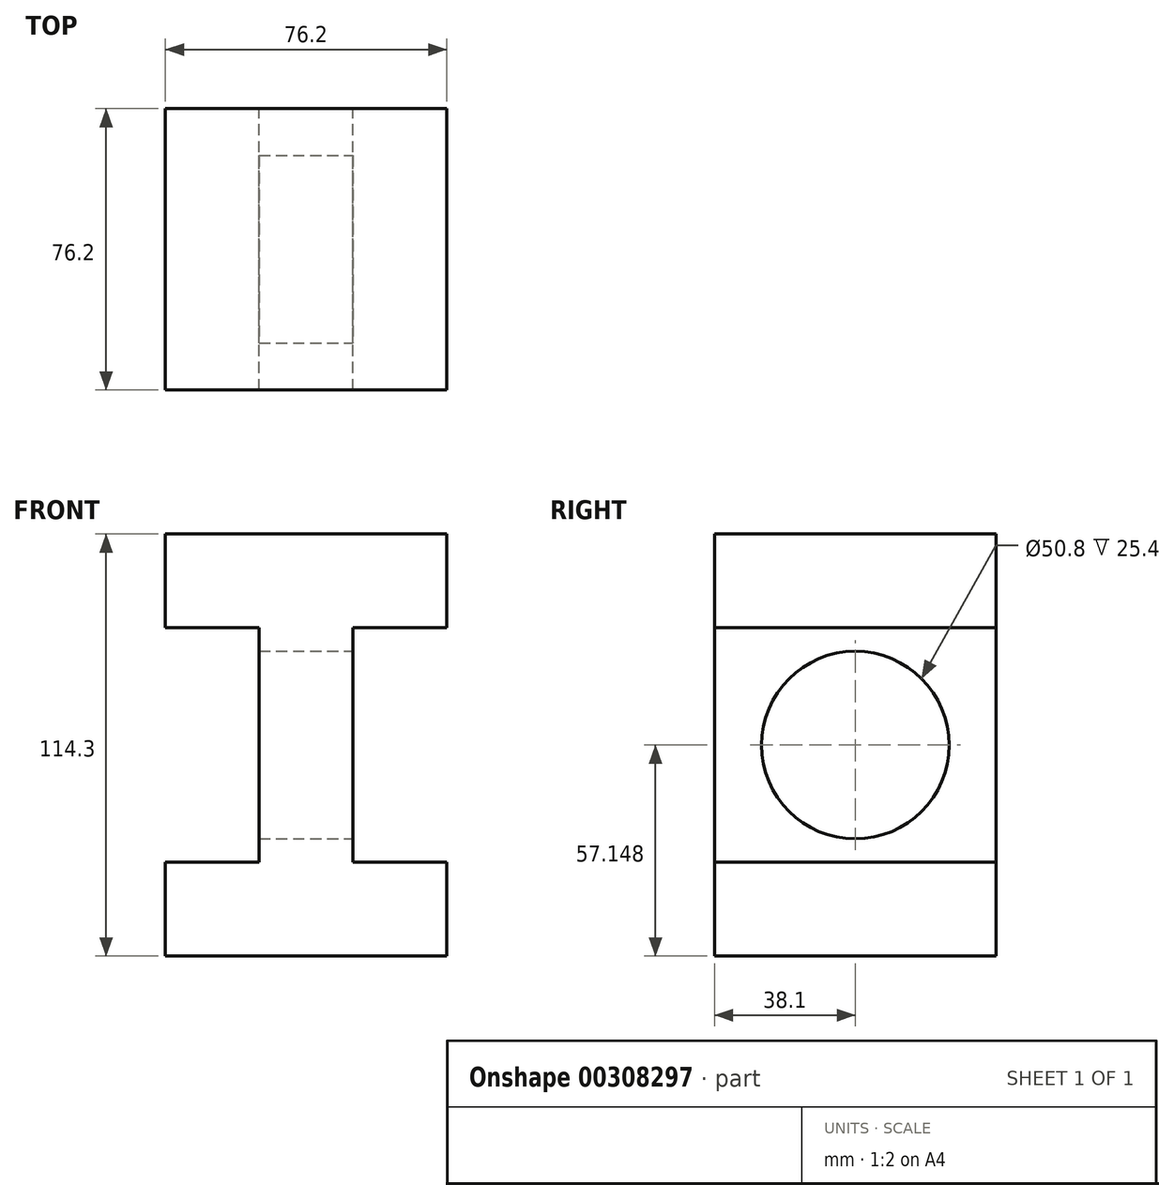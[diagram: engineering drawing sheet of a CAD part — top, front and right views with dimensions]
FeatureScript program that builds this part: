
annotation { "Feature Type Name" : "Feature", "Feature Type Description" : "" }
export const myFeature = defineFeature(function(context is Context, id is Id, definition is map)
    precondition{}
    {
        {
            var Q0;
            Q0=qCreatedBy(makeId("Front.planeOp"),FACE);
            var sketch = newSketch(context, id + "F0", { "sketchPlane" : qUnion([Q0])});
            skLineSegment(sketch, "E0", {"start": v(-40.08, -37.01) * mm, "end": v(36.12, -37.01) * mm});
            skLineSegment(sketch, "E1", {"start": v(36.12, -37.01) * mm, "end": v(36.12, -11.61) * mm});
            skLineSegment(sketch, "E2", {"start": v(36.12, -11.61) * mm, "end": v(10.72, -11.61) * mm});
            skLineSegment(sketch, "E3", {"start": v(10.72, -11.61) * mm, "end": v(10.72, 51.89) * mm});
            skLineSegment(sketch, "E4", {"start": v(10.72, 51.89) * mm, "end": v(36.12, 51.89) * mm});
            skLineSegment(sketch, "E5", {"start": v(36.12, 51.89) * mm, "end": v(36.12, 77.29) * mm});
            skPoint(sketch, "E5.endSnap0", {"position": v(36.12, -24.31) * mm});
            skLineSegment(sketch, "E6", {"start": v(36.12, 77.29) * mm, "end": v(-40.08, 77.29) * mm});
            skLineSegment(sketch, "E7", {"start": v(-40.08, 77.29) * mm, "end": v(-40.08, 51.89) * mm});
            skLineSegment(sketch, "E8", {"start": v(-40.08, 51.89) * mm, "end": v(-14.68, 51.89) * mm});
            skLineSegment(sketch, "E9", {"start": v(-14.68, 51.89) * mm, "end": v(-14.68, -11.61) * mm});
            skLineSegment(sketch, "E10", {"start": v(-14.68, -11.61) * mm, "end": v(-40.08, -11.61) * mm});
            skLineSegment(sketch, "E11", {"start": v(-40.08, -11.61) * mm, "end": v(-40.08, -37.01) * mm});
            skSolve(sketch);
        }
        {
            var Q0;
            Q0=makeQuery(id+"F0.imprint","IMPRINT",FACE,{"disambiguationData":[TD([[makeQuery(id+"F0.imprint","IMPRINT",EDGE,{"derivedFrom":sQuery(id+"F0.wireOp",EDGE,"E0")}),1.0]])]});
            extrude(context, id + "F1", {"entities" : qUnion([Q0]), "depth" : 76.2 * mm});
        }
        {
            var Q0;
            Q0=makeQuery(id+"F1.opExtrude","SWEPT_FACE",FACE,{"disambiguationData":[OSD([sQuery(id+"F0.wireOp",EDGE,"E3")])]});
            var sketch = newSketch(context, id + "F2", { "sketchPlane" : qUnion([Q0])});
            skCircle(sketch, "E12", {"center": v(-38.1, 20.14) * mm, "radius": 25.4 * mm});
            skPoint(sketch, "E12.centerSnap0", {"position": v(-38.1, 51.89) * mm});
            skPoint(sketch, "E12.centerSnap1", {"position": v(-76.2, 20.14) * mm});
            skSolve(sketch);
        }
        {
            var Q0;
            Q0=makeQuery(id+"F2.imprint","IMPRINT",FACE,{"disambiguationData":[TD([[makeQuery(id+"F2.imprint","IMPRINT",EDGE,{"derivedFrom":sQuery(id+"F2.wireOp",EDGE,"E12")}),1.0]])]});
            extrude(context, id + "F3", {"entities" : qUnion([Q0]), "operationType" : NewBodyOperationType.REMOVE, "oppositeDirection" : true, "depth" : 25.4 * mm});
        }
    });
